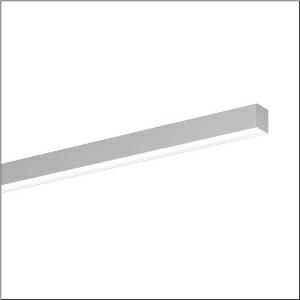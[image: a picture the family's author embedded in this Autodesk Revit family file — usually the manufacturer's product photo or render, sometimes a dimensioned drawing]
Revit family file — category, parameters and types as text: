
# Revit family: silica_21_51mx20db42sb
name_source: partatom
category: Lighting Fixtures
units: mm (PartAtom-declared; Revit-internal decimal feet)

## family parameters
Cut with Voids When Loaded = No
Host = Face
Light Source = No
Part Type = Normal
Room Calculation Point = No
Round Connector Dimension = Use Diameter
Shared = No

## types (1)
- --- (1 x LED, 3000 lm, 19 W, 4000K)
    Apparent Load = 19 VA
    CIE Flux Codes = 48 79 96 100 100
    Color Rendering = 80
    Color Temperature = 4000K
    Default Elevation = 1800 mm
    Description = Silica 21, office luminaire, primary optical cover: cover, of PMMA, opal, light emission: direct distribution, primary light characteristic: symmetric, installation type: surface-mounted, LED, rated luminous flux: 3.000lm, luminous efficacy: 158lm/W, light colour: 840, colour temperature: 4000K, control gear: DALI 2, with terminal, 3+2-pole, max. 2.5mm², mains connection: 220..240V, AC, 50/60Hz, rated input power: 19W, luminaire housing, of aluminium, metallic grey (RAL 9006), length: 1.504mm, width: 53mm, height: 53mm, protection rating (complete): IP20, insulation class (complete): insulation class I (protective earthing), certification: CE, permissible operating ambient temperature: 0..+35°C, standard: EN 50419, packaging unit: 1 piece
    Height = 53 mm
    Lamp = 1 x LED
    Lamp Light Flux = 3000 lm
    Lamp Power = 19 W
    Lamp count = 1
    Length = 1504 mm
    Luminous efficacy = 158 lm/W
    Manufacturer = Siteco
    ModVariant = No
    Model = 51MX20DB42SB
    Mounting Place = Ceiling
    Mounting Type = Surface mounted
    Number of Poles = 1
    OnlyDefault = Yes
    Power Factor = 1
    Product Name = Silica 21
    Product group = office luminaire | ceiling mounted
    ProductGroupID = 301
    Protection Class = Protection class I
    Protection Degree = IP 20
    RLX_Detail_Level = 1
    RLX_Emergency_Light_Flux = 0 lm
    RLX_Emergency_Type = 0
    RLX_Emergency_Type_DB = No
    RlxData = <blob elided: 26261 chars, md5=661f5952>
    Socket = socket
    Standby Power = 0 W
    System Light Flux = 3000 lm
    System Power = 19 W
    Type Comments = factory setting: luminous flux: 100 % | dim-lin: 254 | 218 mA
    Type Image = l_1335933.jpg
    URL = http://relux.com
    VarID = @adj_118177
    Voltage = 0 V
    Weight = 0.00 kg
    Width = 53 mm

## geometry (parser evidence)
native form markers: Blend x4, Sweep x9
no freeform markers — native parametric forms only
